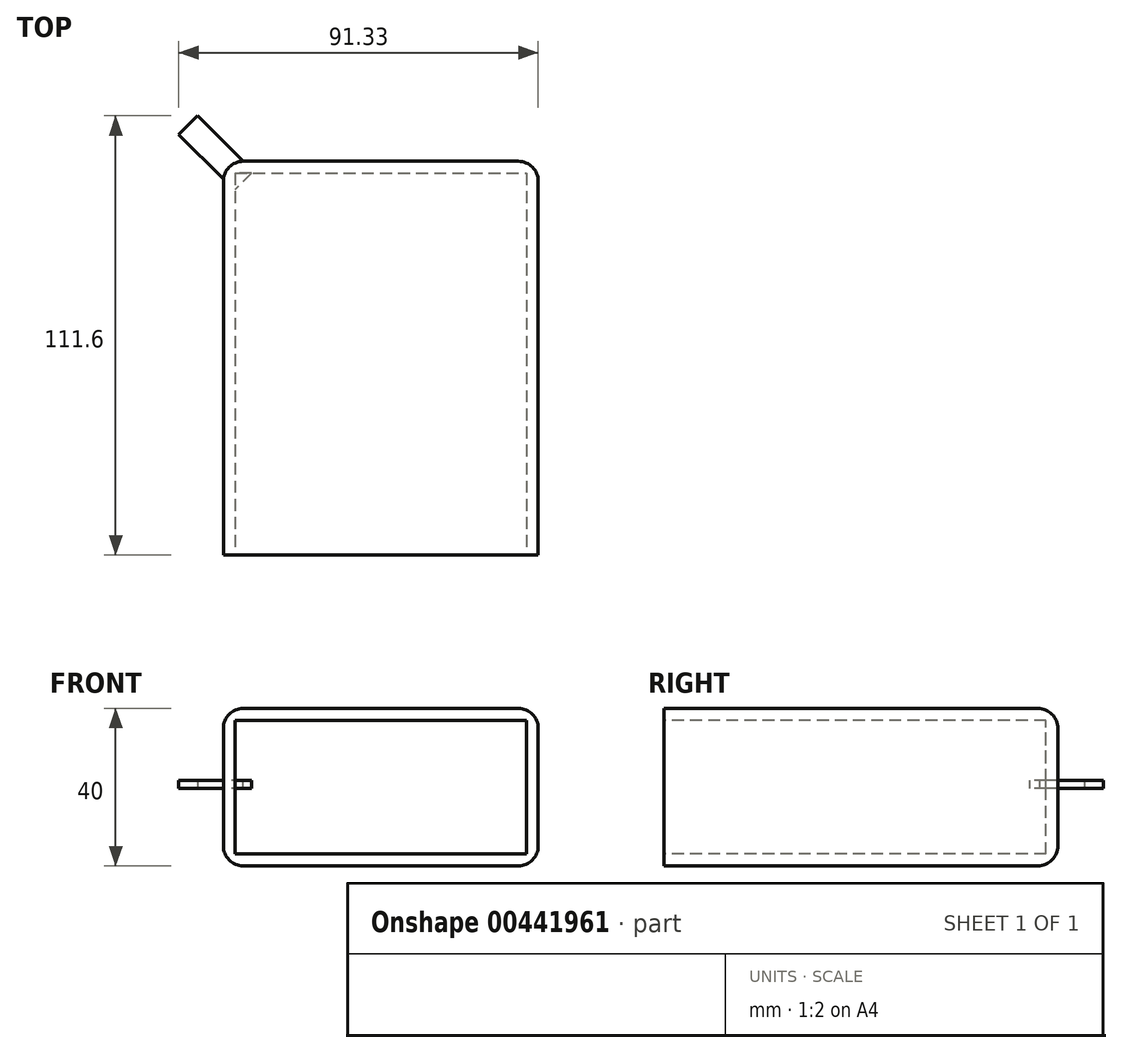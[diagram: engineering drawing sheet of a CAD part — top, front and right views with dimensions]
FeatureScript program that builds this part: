
annotation { "Feature Type Name" : "Feature", "Feature Type Description" : "" }
export const myFeature = defineFeature(function(context is Context, id is Id, definition is map)
    precondition{}
    {
        {
            var Q0;
            Q0=qCreatedBy(makeId("Front.planeOp"),FACE);
            var sketch = newSketch(context, id + "F0", { "sketchPlane" : qUnion([Q0])});
            skLineSegment(sketch, "E0.bottom", {"start": v(0, 0) * mm, "end": v(80, 0) * mm});
            skLineSegment(sketch, "E0.top", {"start": v(0, 40) * mm, "end": v(80, 40) * mm});
            skLineSegment(sketch, "E0.left", {"start": v(0, 0) * mm, "end": v(0, 40) * mm});
            skLineSegment(sketch, "E0.right", {"start": v(80, 0) * mm, "end": v(80, 40) * mm});
            skSolve(sketch);
        }
        {
            var Q0;
            Q0 = qSketchRegion(id + "F0", true);
            extrude(context, id + "F1", {"entities" : qUnion([Q0]), "oppositeDirection" : true, "depth" : 100 * mm});
        }
        {
            var Q0;
            Q0=makeQuery(id+"F1.opExtrude","CAP_FACE",FACE,{"disambiguationData":[OSD([sQuery(id+"F0.wireOp",EDGE,"E0.bottom"),sQuery(id+"F0.wireOp",EDGE,"E0.top"),sQuery(id+"F0.wireOp",EDGE,"E0.left"),sQuery(id+"F0.wireOp",EDGE,"E0.right")])],"isStart":true});
            shell(context, id + "F2", {"entities" : qUnion([Q0]), "thickness" : 3 * mm});
        }
        {
            var Q0;
            Q0=makeQuery(id+"F1.opExtrude","SWEPT_EDGE",EDGE,{"disambiguationData":[OSD([sQuery(id+"F0.wireOp",EDGE,"E0.top"),sQuery(id+"F0.wireOp",EDGE,"E0.left")])]});
            fillet(context, id + "F3", {"entities" : qUnion([Q0]), "radius" : 5.08 * mm, "tangentPropagation" : true, "allowEdgeOverflow" : false});
        }
        {
            var Q0;
            Q0=makeQuery(id+"F1.opExtrude","SWEPT_EDGE",EDGE,{"disambiguationData":[OSD([sQuery(id+"F0.wireOp",EDGE,"E0.top"),sQuery(id+"F0.wireOp",EDGE,"E0.right")])]});
            fillet(context, id + "F4", {"entities" : qUnion([Q0]), "radius" : 5.08 * mm, "tangentPropagation" : true, "allowEdgeOverflow" : false});
        }
        {
            var Q0;
            Q0=makeQuery(id+"F1.opExtrude","CAP_EDGE",EDGE,{"disambiguationData":[OSD([sQuery(id+"F0.wireOp",EDGE,"E0.top")])],"isStart":false});
            fillet(context, id + "F5", {"entities" : qUnion([Q0]), "radius" : 5.08 * mm, "tangentPropagation" : true, "allowEdgeOverflow" : false});
        }
        {
            var Q0;
            Q0=makeQuery(id+"F1.opExtrude","CAP_EDGE",EDGE,{"disambiguationData":[OSD([sQuery(id+"F0.wireOp",EDGE,"E0.bottom")])],"isStart":false});
            fillet(context, id + "F6", {"entities" : qUnion([Q0]), "radius" : 5.08 * mm, "tangentPropagation" : true, "allowEdgeOverflow" : false});
        }
        {
            var Q0;
            Q0=makeQuery(id+"F5.opFillet","BLEND_FACE",FACE,{"disambiguationData":[OSD([sQuery(id+"F0.wireOp",EDGE,"E0.left")])]});
            cPlane(context, id + "F7", {"entities" : qUnion([Q0]), "cplaneType" : CPlaneType.LINE_ANGLE, "offset" : 25.4 * mm, "angle" : 45 * degree, "oppositeDirection" : true, "width" : 152.4 * mm, "height" : 152.4 * mm});
        }
        {
            var Q0;
            Q0=qCreatedBy(id+"F7.planeOp",FACE);
            var sketch = newSketch(context, id + "F8", { "sketchPlane" : qUnion([Q0])});
            skLineSegment(sketch, "E1.bottom", {"start": v(74.3, 21.68) * mm, "end": v(67.5, 21.68) * mm});
            skLineSegment(sketch, "E1.top", {"start": v(74.3, 19.68) * mm, "end": v(67.5, 19.68) * mm});
            skLineSegment(sketch, "E1.left", {"start": v(74.3, 21.68) * mm, "end": v(74.3, 19.68) * mm});
            skLineSegment(sketch, "E1.right", {"start": v(67.5, 21.68) * mm, "end": v(67.5, 19.68) * mm});
            skSolve(sketch);
        }
        {
            var Q0;
            Q0 = qSketchRegion(id + "F8", true);
            extrude(context, id + "F9", {"entities" : qUnion([Q0]), "operationType" : NewBodyOperationType.ADD, "oppositeDirection" : true, "depth" : 20 * mm});
        }
    });
